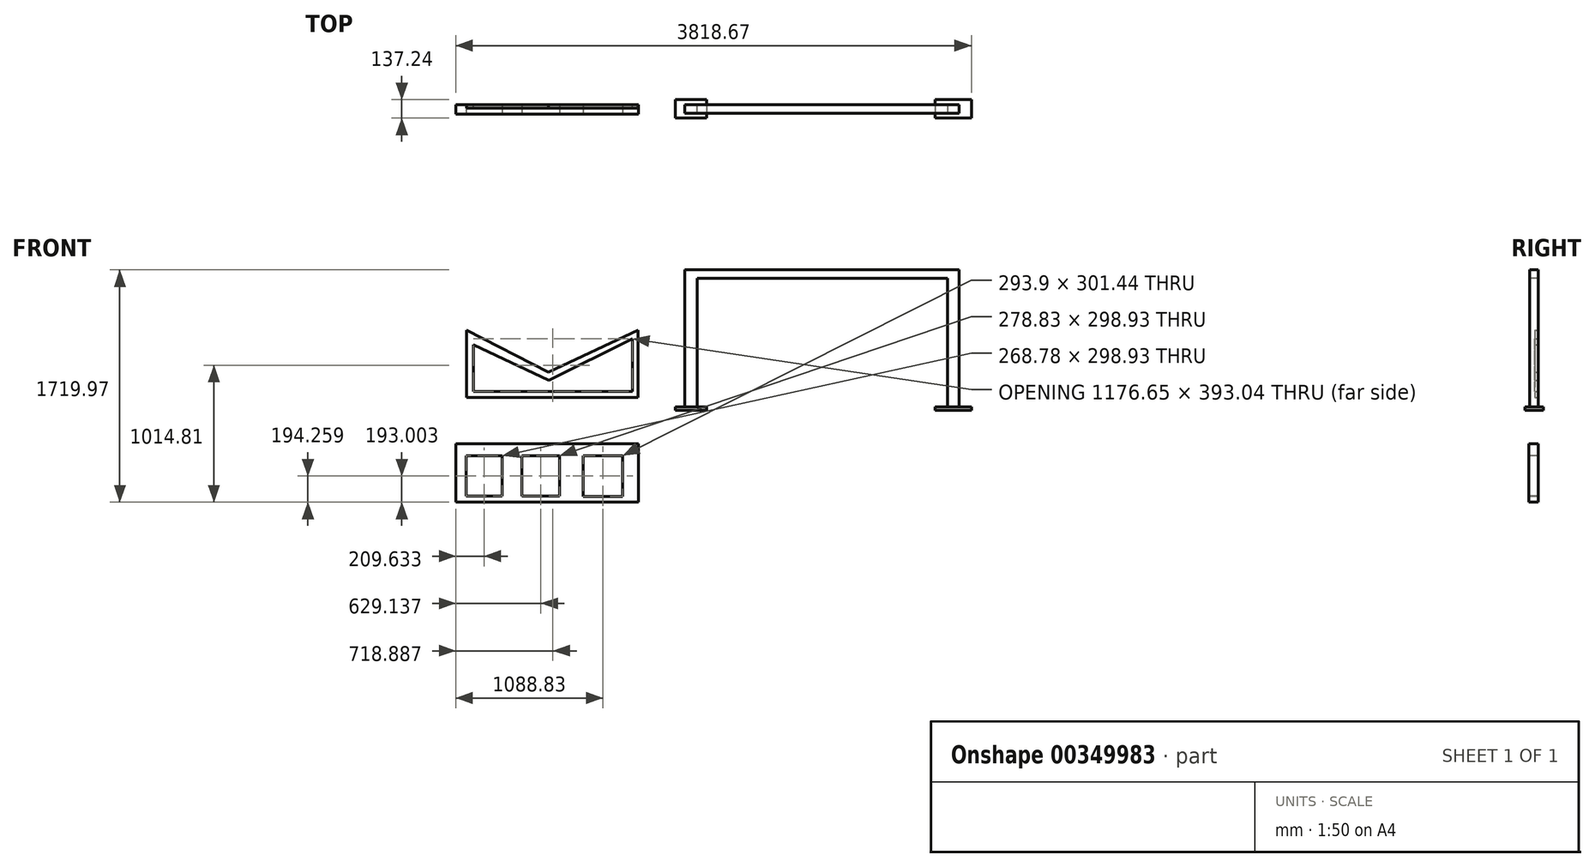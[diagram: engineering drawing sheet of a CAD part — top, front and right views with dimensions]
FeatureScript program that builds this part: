
annotation { "Feature Type Name" : "Feature", "Feature Type Description" : "" }
export const myFeature = defineFeature(function(context is Context, id is Id, definition is map)
    precondition{}
    {
        {
            var Q0;
            Q0=qCreatedBy(makeId("Front.planeOp"),FACE);
            var sketch = newSketch(context, id + "F0", { "sketchPlane" : qUnion([Q0])});
            skLineSegment(sketch, "E0", {"start": v(-735.72, 249.33) * mm, "end": v(-735.72, -185.46) * mm});
            skLineSegment(sketch, "E1", {"start": v(-735.72, -185.46) * mm, "end": v(534.28, -185.46) * mm});
            skLineSegment(sketch, "E2", {"start": v(534.28, -185.46) * mm, "end": v(534.28, 310.74) * mm});
            skLineSegment(sketch, "E3", {"start": v(534.28, 310.74) * mm, "end": v(-128.97, 0) * mm});
            skLineSegment(sketch, "E4", {"start": v(-128.97, 0) * mm, "end": v(-735.72, 310.74) * mm});
            skLineSegment(sketch, "E5", {"start": v(-735.72, 310.74) * mm, "end": v(-735.72, 249.33) * mm});
            skLineSegment(sketch, "E6", {"start": v(-684.13, 205.12) * mm, "end": v(-684.13, -143.7) * mm});
            skLineSegment(sketch, "E7", {"start": v(-684.13, -143.7) * mm, "end": v(492.52, -143.7) * mm});
            skLineSegment(sketch, "E8", {"start": v(492.52, -143.7) * mm, "end": v(492.52, 249.33) * mm});
            skLineSegment(sketch, "E9", {"start": v(492.52, 249.33) * mm, "end": v(-126.5, -60.18) * mm});
            skLineSegment(sketch, "E10", {"start": v(-126.5, -60.18) * mm, "end": v(-684.13, 205.12) * mm});
            skLineSegment(sketch, "E11", {"start": v(-341.85, 42.27) * mm, "end": v(-341.85, -143.7) * mm});
            skLineSegment(sketch, "E12", {"start": v(-341.85, -143.7) * mm, "end": v(77.38, -143.7) * mm});
            skLineSegment(sketch, "E13", {"start": v(77.38, -143.7) * mm, "end": v(77.38, 41.76) * mm});
            skCircle(sketch, "E14", {"center": v(-268.98, -82.3) * mm, "radius": 23.17 * mm});
            skCircle(sketch, "E15", {"center": v(0, -87.2) * mm, "radius": 25.32 * mm});
            skSolve(sketch);
        }
        {
            var Q0;
            Q0=makeQuery(id+"F0.imprint","IMPRINT",FACE,{"disambiguationData":[TD([[makeQuery(id+"F0.imprint","IMPRINT",EDGE,{"derivedFrom":sQuery(id+"F0.wireOp",EDGE,"E0")}),1.0]])]});
            extrude(context, id + "F1", {"entities" : qUnion([Q0]), "depth" : 25.4 * mm, "offsetDistance" : 25.4 * mm});
        }
        {
            var Q0;
            Q0=qCreatedBy(makeId("Front.planeOp"),FACE);
            var sketch = newSketch(context, id + "F2", { "sketchPlane" : qUnion([Q0])});
            skLineSegment(sketch, "E16.bottom", {"start": v(-814.69, -530.2) * mm, "end": v(539.04, -530.2) * mm});
            skLineSegment(sketch, "E16.top", {"start": v(-814.69, -962) * mm, "end": v(539.04, -962) * mm});
            skLineSegment(sketch, "E16.left", {"start": v(-814.69, -530.2) * mm, "end": v(-814.69, -962) * mm});
            skLineSegment(sketch, "E16.right", {"start": v(539.04, -530.2) * mm, "end": v(539.04, -962) * mm});
            skSolve(sketch);
        }
        {
            var Q0;
            Q0 = qSketchRegion(id + "F2", true);
            extrude(context, id + "F3", {"entities" : qUnion([Q0]), "depth" : 71.12 * mm, "offsetDistance" : 25.4 * mm});
        }
        {
            var Q0;
            Q0=makeQuery(id+"F3.opExtrude","CAP_FACE",FACE,{"disambiguationData":[OSD([sQuery(id+"F2.wireOp",EDGE,"E16.bottom"),sQuery(id+"F2.wireOp",EDGE,"E16.top"),sQuery(id+"F2.wireOp",EDGE,"E16.left"),sQuery(id+"F2.wireOp",EDGE,"E16.right")])],"isStart":false});
            var sketch = newSketch(context, id + "F4", { "sketchPlane" : qUnion([Q0])});
            skLineSegment(sketch, "E17.bottom", {"start": v(-739.45, -618.28) * mm, "end": v(-470.66, -618.28) * mm});
            skLineSegment(sketch, "E17.top", {"start": v(-739.45, -917.2) * mm, "end": v(-470.66, -917.2) * mm});
            skLineSegment(sketch, "E17.left", {"start": v(-739.45, -618.28) * mm, "end": v(-739.45, -917.2) * mm});
            skLineSegment(sketch, "E17.right", {"start": v(-470.66, -618.28) * mm, "end": v(-470.66, -917.2) * mm});
            skLineSegment(sketch, "E18.bottom", {"start": v(-324.97, -618.28) * mm, "end": v(-46.14, -618.28) * mm});
            skLineSegment(sketch, "E18.top", {"start": v(-324.97, -917.2) * mm, "end": v(-46.14, -917.2) * mm});
            skLineSegment(sketch, "E18.left", {"start": v(-324.97, -618.28) * mm, "end": v(-324.97, -917.2) * mm});
            skLineSegment(sketch, "E18.right", {"start": v(-46.14, -618.28) * mm, "end": v(-46.14, -917.2) * mm});
            skLineSegment(sketch, "E19.bottom", {"start": v(127.2, -618.28) * mm, "end": v(421.1, -618.28) * mm});
            skLineSegment(sketch, "E19.top", {"start": v(127.2, -919.72) * mm, "end": v(421.1, -919.72) * mm});
            skLineSegment(sketch, "E19.left", {"start": v(127.2, -618.28) * mm, "end": v(127.2, -919.72) * mm});
            skLineSegment(sketch, "E19.right", {"start": v(421.1, -618.28) * mm, "end": v(421.1, -919.72) * mm});
            skSolve(sketch);
        }
        {
            var Q0;
            Q0 = qSketchRegion(id + "F4", true);
            extrude(context, id + "F5", {"entities" : qUnion([Q0]), "operationType" : NewBodyOperationType.REMOVE, "oppositeDirection" : true, "depth" : 132.08 * mm, "offsetDistance" : 25.4 * mm});
        }
        {
            var Q0;
            Q0=qCreatedBy(makeId("Front.planeOp"),FACE);
            var sketch = newSketch(context, id + "F6", { "sketchPlane" : qUnion([Q0])});
            skLineSegment(sketch, "E20.bottom", {"start": v(881.61, 757.97) * mm, "end": v(2913.61, 757.97) * mm});
            skLineSegment(sketch, "E20.top", {"start": v(881.61, -258.03) * mm, "end": v(2913.61, -258.03) * mm});
            skLineSegment(sketch, "E20.left", {"start": v(881.61, 757.97) * mm, "end": v(881.61, -258.03) * mm});
            skLineSegment(sketch, "E20.right", {"start": v(2913.61, 757.97) * mm, "end": v(2913.61, -258.03) * mm});
            skSolve(sketch);
        }
        {
            var Q0;
            Q0 = qSketchRegion(id + "F6", true);
            extrude(context, id + "F7", {"entities" : qUnion([Q0]), "depth" : 63.5 * mm, "offsetDistance" : 25.4 * mm});
        }
        {
            var Q0;
            Q0=makeQuery(id+"F7.opExtrude","CAP_FACE",FACE,{"disambiguationData":[OSD([sQuery(id+"F6.wireOp",EDGE,"E20.bottom"),sQuery(id+"F6.wireOp",EDGE,"E20.top"),sQuery(id+"F6.wireOp",EDGE,"E20.left"),sQuery(id+"F6.wireOp",EDGE,"E20.right")])],"isStart":false});
            var sketch = newSketch(context, id + "F8", { "sketchPlane" : qUnion([Q0])});
            skLineSegment(sketch, "E21.bottom", {"start": v(972.27, -295.52) * mm, "end": v(2826.47, -295.52) * mm});
            skLineSegment(sketch, "E21.top", {"start": v(972.27, 695.08) * mm, "end": v(2826.47, 695.08) * mm});
            skLineSegment(sketch, "E21.left", {"start": v(972.27, -295.52) * mm, "end": v(972.27, 695.08) * mm});
            skLineSegment(sketch, "E21.right", {"start": v(2826.47, -295.52) * mm, "end": v(2826.47, 695.08) * mm});
            skSolve(sketch);
        }
        {
            var Q0;
            Q0 = qSketchRegion(id + "F8", true);
            extrude(context, id + "F9", {"entities" : qUnion([Q0]), "operationType" : NewBodyOperationType.REMOVE, "oppositeDirection" : true, "depth" : 276.86 * mm, "offsetDistance" : 25.4 * mm});
        }
        {
            var Q0;
            {var subQ1=sQuery(id+"F6.wireOp",EDGE,"E20.left");var subQ2=sQuery(id+"F6.wireOp",EDGE,"E20.top");Q0=makeQuery(id+"F9.boolean.opBoolean","SPLIT",FACE,{"disambiguationData":[TD([makeQuery(id+"F7.opExtrude","SWEPT_FACE",FACE,{"disambiguationData":[OSD([subQ1])]})])],"derivedFrom":makeQuery(id+"F7.opExtrude","SWEPT_FACE",FACE,{"disambiguationData":[OSD([subQ2])]})});}
            var sketch = newSketch(context, id + "F10", { "sketchPlane" : qUnion([Q0])});
            skLineSegment(sketch, "E22.bottom", {"start": v(1043.13, -36.57) * mm, "end": v(810.74, -36.57) * mm});
            skLineSegment(sketch, "E22.top", {"start": v(1043.13, 100.07) * mm, "end": v(810.74, 100.07) * mm});
            skLineSegment(sketch, "E22.left", {"start": v(1043.13, -36.57) * mm, "end": v(1043.13, 100.07) * mm});
            skLineSegment(sketch, "E22.right", {"start": v(810.74, -36.57) * mm, "end": v(810.74, 100.07) * mm});
            skPoint(sketch, "E22.middle", {"position": v(926.94, 31.75) * mm});
            skPoint(sketch, "E22.middle.positionSnap0", {"position": v(972.27, 31.75) * mm});
            skPoint(sketch, "E22.middle.positionSnap1", {"position": v(926.94, 63.5) * mm});
            skPoint(sketch, "E22.centerSnap0", {"position": v(972.27, 31.75) * mm});
            skPoint(sketch, "E22.centerSnap1", {"position": v(926.94, 63.5) * mm});
            skPoint(sketch, "E23.middle", {"position": v(2297.64, 33.56) * mm});
            skSolve(sketch);
        }
        {
            var Q0;
            Q0 = qSketchRegion(id + "F10", true);
            extrude(context, id + "F11", {"entities" : qUnion([Q0]), "operationType" : NewBodyOperationType.ADD, "depth" : 25.4 * mm, "offsetDistance" : 25.4 * mm});
        }
        {
            var Q0;
            {var subQ0=sQuery(id+"F6.wireOp",EDGE,"E20.right");var subQ2=sQuery(id+"F6.wireOp",EDGE,"E20.top");Q0=makeQuery(id+"F9.boolean.opBoolean","SPLIT",FACE,{"disambiguationData":[TD([makeQuery(id+"F7.opExtrude","SWEPT_FACE",FACE,{"disambiguationData":[OSD([subQ0])]})])],"derivedFrom":makeQuery(id+"F7.opExtrude","SWEPT_FACE",FACE,{"disambiguationData":[OSD([subQ2])]})});}
            var sketch = newSketch(context, id + "F12", { "sketchPlane" : qUnion([Q0])});
            skLineSegment(sketch, "E24.bottom", {"start": v(3003.98, -36.87) * mm, "end": v(2736.1, -36.87) * mm});
            skLineSegment(sketch, "E24.top", {"start": v(3003.98, 100.37) * mm, "end": v(2736.1, 100.37) * mm});
            skLineSegment(sketch, "E24.left", {"start": v(3003.98, -36.87) * mm, "end": v(3003.98, 100.37) * mm});
            skLineSegment(sketch, "E24.right", {"start": v(2736.1, -36.87) * mm, "end": v(2736.1, 100.37) * mm});
            skPoint(sketch, "E24.middle", {"position": v(2870.04, 31.75) * mm});
            skPoint(sketch, "E24.middle.positionSnap0", {"position": v(2870.04, 0) * mm});
            skPoint(sketch, "E24.middle.positionSnap1", {"position": v(2826.47, 31.75) * mm});
            skPoint(sketch, "E24.centerSnap0", {"position": v(2870.04, 0) * mm});
            skPoint(sketch, "E24.centerSnap1", {"position": v(2826.47, 31.75) * mm});
            skSolve(sketch);
        }
        {
            var Q0;
            Q0 = qSketchRegion(id + "F12", true);
            extrude(context, id + "F13", {"entities" : qUnion([Q0]), "operationType" : NewBodyOperationType.ADD, "depth" : 25.4 * mm, "offsetDistance" : 25.4 * mm});
        }
    });
